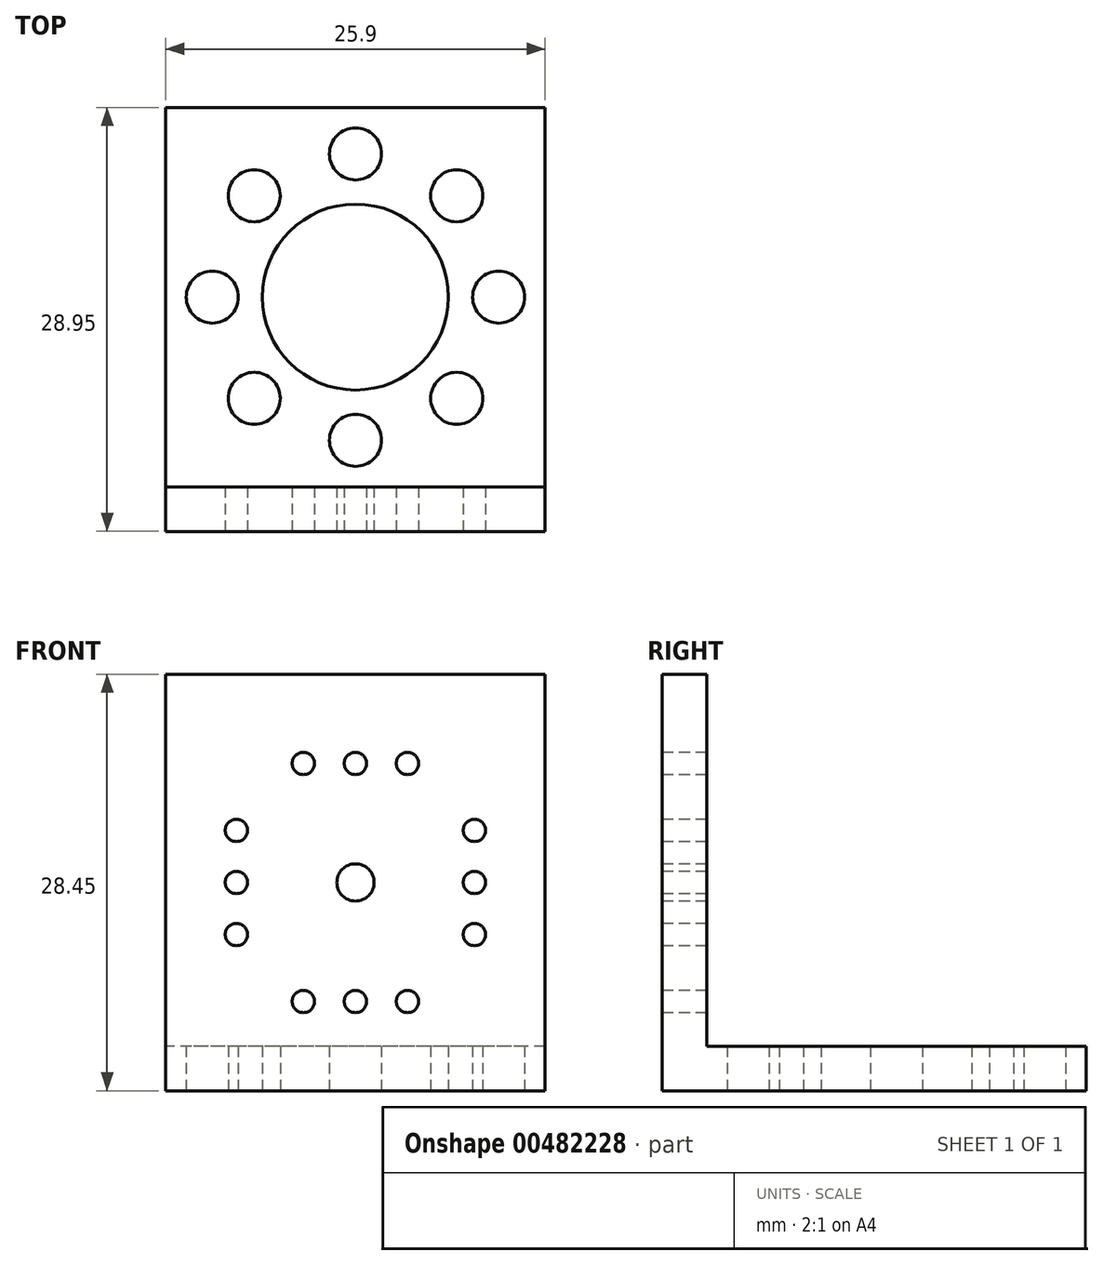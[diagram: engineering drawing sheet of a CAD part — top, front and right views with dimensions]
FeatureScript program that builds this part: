
annotation { "Feature Type Name" : "Feature", "Feature Type Description" : "" }
export const myFeature = defineFeature(function(context is Context, id is Id, definition is map)
    precondition{}
    {
        {
            var Q0;
            Q0=qCreatedBy(makeId("Top.planeOp"),FACE);
            var sketch = newSketch(context, id + "F0", { "sketchPlane" : qUnion([Q0])});
            skLineSegment(sketch, "E0.bottom", {"start": v(12.95, -12.95) * mm, "end": v(-12.95, -12.95) * mm});
            skLineSegment(sketch, "E0.top", {"start": v(12.95, 12.95) * mm, "end": v(-12.95, 12.95) * mm});
            skLineSegment(sketch, "E0.left", {"start": v(12.95, -12.95) * mm, "end": v(12.95, 12.95) * mm});
            skLineSegment(sketch, "E0.right", {"start": v(-12.95, -12.95) * mm, "end": v(-12.95, 12.95) * mm});
            skPoint(sketch, "E0.middle", {"position": v(0, 0) * mm});
            skCircle(sketch, "E1", {"center": v(0, 0) * mm, "radius": 6.35 * mm});
            skCircle(sketch, "E2", {"center": v(0, 9.78) * mm, "radius": 1.78 * mm});
            skCircle(sketch, "E3", {"center": v(9.78, 0) * mm, "radius": 1.78 * mm});
            skCircle(sketch, "E4", {"center": v(0, -9.78) * mm, "radius": 1.78 * mm});
            skCircle(sketch, "E5", {"center": v(-9.78, 0) * mm, "radius": 1.78 * mm});
            skCircle(sketch, "E6", {"center": v(-6.91, 6.91) * mm, "radius": 1.78 * mm});
            skCircle(sketch, "E7", {"center": v(6.91, 6.91) * mm, "radius": 1.78 * mm});
            skCircle(sketch, "E8", {"center": v(6.91, -6.91) * mm, "radius": 1.78 * mm});
            skCircle(sketch, "E9", {"center": v(-6.91, -6.91) * mm, "radius": 1.78 * mm});
            skLineSegment(sketch, "E10", {"start": v(6.91, 6.91) * mm, "end": v(0, 0) * mm});
            skLineSegment(sketch, "E11", {"start": v(-6.91, -6.91) * mm, "end": v(0, 0) * mm});
            skLineSegment(sketch, "E12", {"start": v(-6.91, 6.91) * mm, "end": v(0, 0) * mm});
            skLineSegment(sketch, "E13", {"start": v(0, 0) * mm, "end": v(6.91, -6.91) * mm});
            skSolve(sketch);
        }
        {
            var Q0;
            Q0=makeQuery(id+"F0.imprint","IMPRINT",FACE,{"disambiguationData":[TD([[makeQuery(id+"F0.imprint","IMPRINT",EDGE,{"derivedFrom":sQuery(id+"F0.wireOp",EDGE,"E0.bottom")}),-1.0]])]});
            extrude(context, id + "F1", {"entities" : qUnion([Q0]), "depth" : 3.05 * mm, "offsetDistance" : 25.4 * mm});
        }
        {
            var Q0;
            Q0=makeQuery(id+"F1.opExtrude","CAP_FACE",FACE,{"disambiguationData":[OSD([sQuery(id+"F0.wireOp",EDGE,"E0.bottom"),sQuery(id+"F0.wireOp",EDGE,"E0.top"),sQuery(id+"F0.wireOp",EDGE,"E0.left"),sQuery(id+"F0.wireOp",EDGE,"E0.right"),sQuery(id+"F0.wireOp",EDGE,"E1"),sQuery(id+"F0.wireOp",EDGE,"E2"),sQuery(id+"F0.wireOp",EDGE,"E3"),sQuery(id+"F0.wireOp",EDGE,"E4"),sQuery(id+"F0.wireOp",EDGE,"E5"),sQuery(id+"F0.wireOp",EDGE,"E6"),sQuery(id+"F0.wireOp",EDGE,"E7"),sQuery(id+"F0.wireOp",EDGE,"E8"),sQuery(id+"F0.wireOp",EDGE,"E9")])],"isStart":true});
            var sketch = newSketch(context, id + "F2", { "sketchPlane" : qUnion([Q0])});
            skLineSegment(sketch, "E14.bottom", {"start": v(-12.95, 12.95) * mm, "end": v(12.95, 12.95) * mm});
            skLineSegment(sketch, "E14.top", {"start": v(-12.95, 16) * mm, "end": v(12.95, 16) * mm});
            skLineSegment(sketch, "E14.left", {"start": v(-12.95, 12.95) * mm, "end": v(-12.95, 16) * mm});
            skLineSegment(sketch, "E14.right", {"start": v(12.95, 12.95) * mm, "end": v(12.95, 16) * mm});
            skSolve(sketch);
        }
        {
            var Q0;
            Q0=makeQuery(id+"F2.imprint","IMPRINT",FACE,{"disambiguationData":[TD([[makeQuery(id+"F2.imprint","IMPRINT",EDGE,{"derivedFrom":sQuery(id+"F2.wireOp",EDGE,"E14.bottom")}),-1.0]])]});
            extrude(context, id + "F3", {"entities" : qUnion([Q0]), "operationType" : NewBodyOperationType.ADD, "oppositeDirection" : true, "depth" : 28.45 * mm, "offsetDistance" : 25.4 * mm});
        }
        {
            var Q0;
            Q0=makeQuery(id+"F3.opExtrude","SWEPT_FACE",FACE,{"disambiguationData":[OSD([sQuery(id+"F2.wireOp",EDGE,"E14.top")])]});
            var sketch = newSketch(context, id + "F4", { "sketchPlane" : qUnion([Q0])});
            skLineSegment(sketch, "E15.bottom", {"start": v(12.95, 0) * mm, "end": v(-12.95, 0) * mm});
            skLineSegment(sketch, "E15.top", {"start": v(12.95, 28.45) * mm, "end": v(-12.95, 28.45) * mm});
            skLineSegment(sketch, "E15.left", {"start": v(12.95, 0) * mm, "end": v(12.95, 28.45) * mm});
            skLineSegment(sketch, "E15.right", {"start": v(-12.95, 0) * mm, "end": v(-12.95, 28.45) * mm});
            skPoint(sketch, "E15.middle", {"position": v(0, 14.22) * mm});
            skCircle(sketch, "E16", {"center": v(0, 14.22) * mm, "radius": 9.97 * mm});
            skCircle(sketch, "E17", {"center": v(0, 14.22) * mm, "radius": 1.27 * mm});
            skCircle(sketch, "E18", {"center": v(0, 22.35) * mm, "radius": 0.76 * mm});
            skCircle(sketch, "E19", {"center": v(0, 6.1) * mm, "radius": 0.76 * mm});
            skCircle(sketch, "E20", {"center": v(8.13, 14.22) * mm, "radius": 0.76 * mm});
            skCircle(sketch, "E21", {"center": v(-8.13, 14.22) * mm, "radius": 0.76 * mm});
            skCircle(sketch, "E22", {"center": v(-8.13, 10.67) * mm, "radius": 0.76 * mm});
            skCircle(sketch, "E23", {"center": v(-8.13, 17.78) * mm, "radius": 0.76 * mm});
            skCircle(sketch, "E24", {"center": v(3.56, 22.35) * mm, "radius": 0.76 * mm});
            skCircle(sketch, "E25", {"center": v(-3.56, 22.35) * mm, "radius": 0.76 * mm});
            skCircle(sketch, "E26", {"center": v(8.13, 17.78) * mm, "radius": 0.76 * mm});
            skCircle(sketch, "E27", {"center": v(8.13, 10.67) * mm, "radius": 0.76 * mm});
            skCircle(sketch, "E28", {"center": v(3.56, 6.1) * mm, "radius": 0.76 * mm});
            skCircle(sketch, "E29", {"center": v(-3.56, 6.1) * mm, "radius": 0.76 * mm});
            skSolve(sketch);
        }
        {
            var Q0;
            Q0=makeQuery(id+"F4.imprint","IMPRINT",FACE,{"disambiguationData":[TD([[makeQuery(id+"F4.imprint","IMPRINT",EDGE,{"derivedFrom":sQuery(id+"F4.wireOp",EDGE,"E21")}),1.0]])]});
            var Q1;
            Q1=makeQuery(id+"F4.imprint","IMPRINT",FACE,{"disambiguationData":[TD([[makeQuery(id+"F4.imprint","IMPRINT",EDGE,{"derivedFrom":sQuery(id+"F4.wireOp",EDGE,"E23")}),1.0]])]});
            var Q2;
            Q2=makeQuery(id+"F4.imprint","IMPRINT",FACE,{"disambiguationData":[TD([[makeQuery(id+"F4.imprint","IMPRINT",EDGE,{"derivedFrom":sQuery(id+"F4.wireOp",EDGE,"E22")}),1.0]])]});
            var Q3;
            Q3=makeQuery(id+"F4.imprint","IMPRINT",FACE,{"disambiguationData":[TD([[makeQuery(id+"F4.imprint","IMPRINT",EDGE,{"derivedFrom":sQuery(id+"F4.wireOp",EDGE,"E29")}),1.0]])]});
            var Q4;
            Q4=makeQuery(id+"F4.imprint","IMPRINT",FACE,{"disambiguationData":[TD([[makeQuery(id+"F4.imprint","IMPRINT",EDGE,{"derivedFrom":sQuery(id+"F4.wireOp",EDGE,"E19")}),1.0]])]});
            var Q5;
            Q5=makeQuery(id+"F4.imprint","IMPRINT",FACE,{"disambiguationData":[TD([[makeQuery(id+"F4.imprint","IMPRINT",EDGE,{"derivedFrom":sQuery(id+"F4.wireOp",EDGE,"E28")}),1.0]])]});
            var Q6;
            Q6=makeQuery(id+"F4.imprint","IMPRINT",FACE,{"disambiguationData":[TD([[makeQuery(id+"F4.imprint","IMPRINT",EDGE,{"derivedFrom":sQuery(id+"F4.wireOp",EDGE,"E27")}),1.0]])]});
            var Q7;
            Q7=makeQuery(id+"F4.imprint","IMPRINT",FACE,{"disambiguationData":[TD([[makeQuery(id+"F4.imprint","IMPRINT",EDGE,{"derivedFrom":sQuery(id+"F4.wireOp",EDGE,"E20")}),1.0]])]});
            var Q8;
            Q8=makeQuery(id+"F4.imprint","IMPRINT",FACE,{"disambiguationData":[TD([[makeQuery(id+"F4.imprint","IMPRINT",EDGE,{"derivedFrom":sQuery(id+"F4.wireOp",EDGE,"E26")}),1.0]])]});
            var Q9;
            Q9=makeQuery(id+"F4.imprint","IMPRINT",FACE,{"disambiguationData":[TD([[makeQuery(id+"F4.imprint","IMPRINT",EDGE,{"derivedFrom":sQuery(id+"F4.wireOp",EDGE,"E24")}),1.0]])]});
            var Q10;
            Q10=makeQuery(id+"F4.imprint","IMPRINT",FACE,{"disambiguationData":[TD([[makeQuery(id+"F4.imprint","IMPRINT",EDGE,{"derivedFrom":sQuery(id+"F4.wireOp",EDGE,"E18")}),1.0]])]});
            var Q11;
            Q11=makeQuery(id+"F4.imprint","IMPRINT",FACE,{"disambiguationData":[TD([[makeQuery(id+"F4.imprint","IMPRINT",EDGE,{"derivedFrom":sQuery(id+"F4.wireOp",EDGE,"E25")}),1.0]])]});
            var Q12;
            Q12=makeQuery(id+"F4.imprint","IMPRINT",FACE,{"disambiguationData":[TD([[makeQuery(id+"F4.imprint","IMPRINT",EDGE,{"derivedFrom":sQuery(id+"F4.wireOp",EDGE,"E17")}),1.0]])]});
            extrude(context, id + "F5", {"entities" : qUnion([Q0, Q1, Q2, Q3, Q4, Q5, Q6, Q7, Q8, Q9, Q10, Q11, Q12]), "operationType" : NewBodyOperationType.REMOVE, "oppositeDirection" : true, "depth" : 25.4 * mm, "offsetDistance" : 25.4 * mm});
        }
    });
